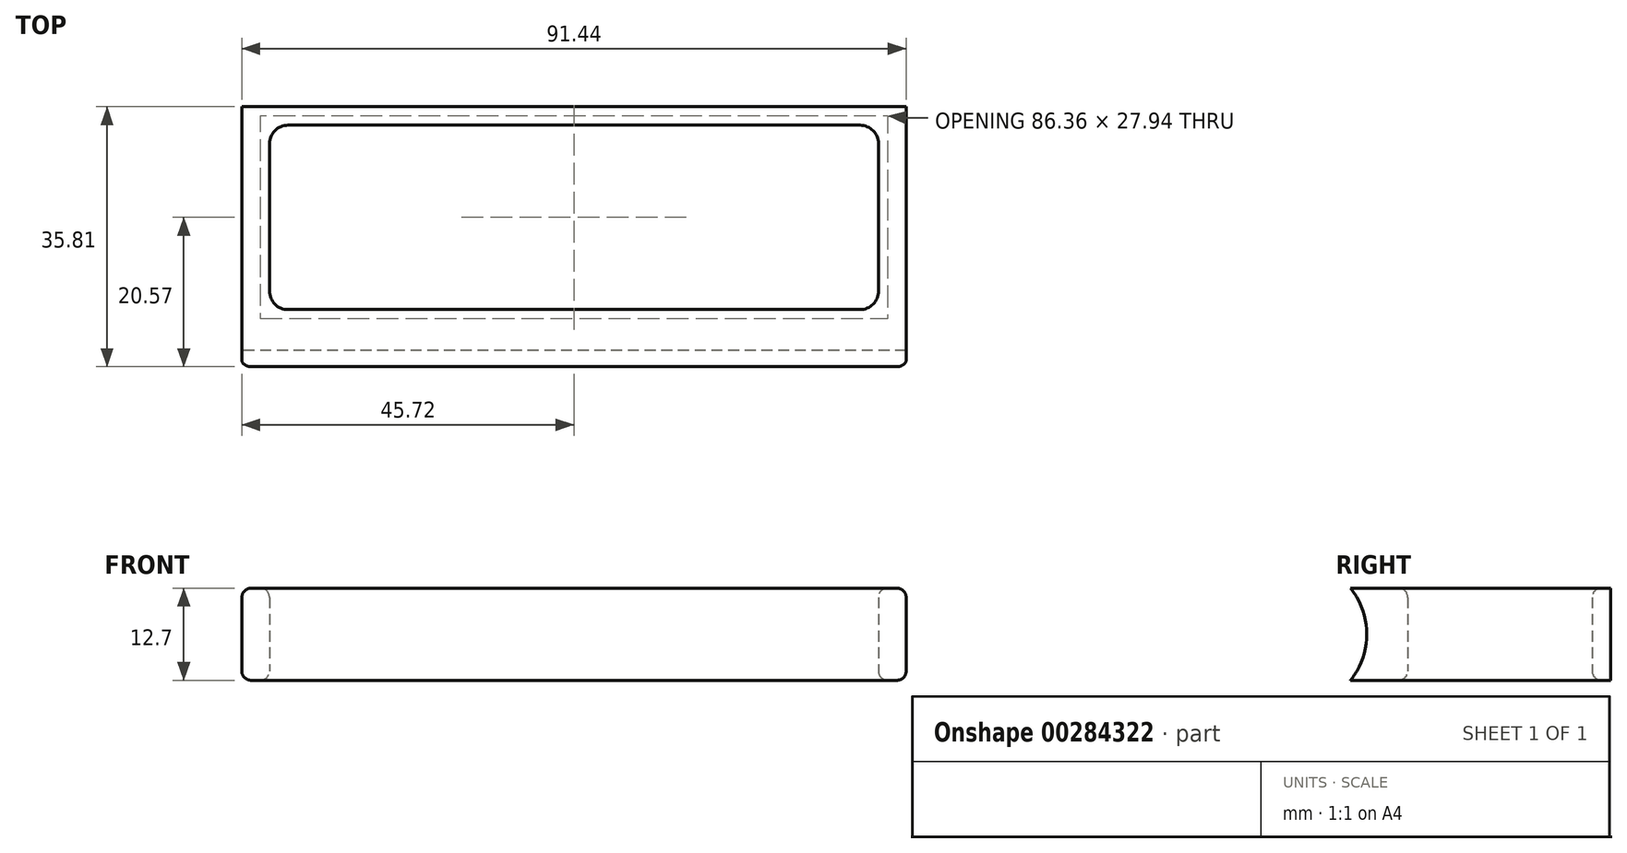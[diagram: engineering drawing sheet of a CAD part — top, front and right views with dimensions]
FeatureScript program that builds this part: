
annotation { "Feature Type Name" : "Feature", "Feature Type Description" : "" }
export const myFeature = defineFeature(function(context is Context, id is Id, definition is map)
    precondition{}
    {
        {
            var Q0;
            Q0=qCreatedBy(makeId("Top.planeOp"),FACE);
            var sketch = newSketch(context, id + "F0", { "sketchPlane" : qUnion([Q0])});
            skLineSegment(sketch, "E0", {"start": v(0, 0) * mm, "end": v(-45.72, 0) * mm});
            skLineSegment(sketch, "E1", {"start": v(0, 0) * mm, "end": v(45.72, 0) * mm});
            skLineSegment(sketch, "E2", {"start": v(-45.72, 0) * mm, "end": v(-45.72, -30.48) * mm});
            skLineSegment(sketch, "E3", {"start": v(-45.72, -30.48) * mm, "end": v(45.72, -30.48) * mm});
            skLineSegment(sketch, "E4", {"start": v(45.72, -30.48) * mm, "end": v(45.72, 0) * mm});
            skLineSegment(sketch, "E5", {"start": v(0, -30.48) * mm, "end": v(0, 0) * mm, "construction": true});
            skLineSegment(sketch, "E6.bottom", {"start": v(-41.91, -2.54) * mm, "end": v(41.91, -2.54) * mm});
            skLineSegment(sketch, "E6.top", {"start": v(-41.91, -27.94) * mm, "end": v(41.91, -27.94) * mm});
            skLineSegment(sketch, "E6.left", {"start": v(-41.91, -2.54) * mm, "end": v(-41.91, -27.94) * mm});
            skLineSegment(sketch, "E6.right", {"start": v(41.91, -2.54) * mm, "end": v(41.91, -27.94) * mm});
            skLineSegment(sketch, "E7", {"start": v(0, -2.54) * mm, "end": v(0, -27.94) * mm, "construction": true});
            skPoint(sketch, "E8", {"position": v(0, -15.24) * mm});
            skLineSegment(sketch, "E9.bottom", {"start": v(-1.27, -2.54) * mm, "end": v(1.27, -2.54) * mm});
            skLineSegment(sketch, "E9.top", {"start": v(-1.27, -27.94) * mm, "end": v(1.27, -27.94) * mm});
            skSolve(sketch);
        }
        {
            var Q0;
            Q0=makeQuery(id+"F0.imprint","IMPRINT",FACE,{"disambiguationData":[TD([[makeQuery(id+"F0.imprint","IMPRINT",EDGE,{"derivedFrom":sQuery(id+"F0.wireOp",EDGE,"E0")}),1.0]])]});
            extrude(context, id + "F1", {"entities" : qUnion([Q0]), "depth" : 12.7 * mm});
        }
        {
            var Q0;
            Q0=makeQuery(id+"F1.opExtrude","SWEPT_FACE",FACE,{"disambiguationData":[OSD([sQuery(id+"F0.wireOp",EDGE,"E4")])]});
            var sketch = newSketch(context, id + "F2", { "sketchPlane" : qUnion([Q0])});
            skLineSegment(sketch, "E10.0.0", {"start": v(-30.48, 0) * mm, "end": v(0, 0) * mm});
            skLineSegment(sketch, "E10.0.1", {"start": v(0, 0) * mm, "end": v(0, 12.7) * mm});
            skLineSegment(sketch, "E10.0.2", {"start": v(0, 12.7) * mm, "end": v(-30.48, 12.7) * mm});
            skLineSegment(sketch, "E10.0.3", {"start": v(-30.48, 12.7) * mm, "end": v(-30.48, 0) * mm});
            skArc(sketch, "E11", {"start": v(-0.6, 9.97) * mm, "mid": v(-0.08, 11.67) * mm, "end": v(-1.52, 12.7) * mm});
            skArc(sketch, "E12", {"start": v(-0.6, 7.56) * mm, "mid": v(0, 8.76) * mm, "end": v(-0.6, 9.97) * mm});
            skArc(sketch, "E13", {"start": v(-0.6, 5.14) * mm, "mid": v(0, 6.35) * mm, "end": v(-0.6, 7.56) * mm});
            skArc(sketch, "E14", {"start": v(-0.6, 2.73) * mm, "mid": v(0, 3.94) * mm, "end": v(-0.6, 5.14) * mm});
            skArc(sketch, "E15", {"start": v(-1.52, 0) * mm, "mid": v(-0.08, 1.03) * mm, "end": v(-0.6, 2.73) * mm});
            skLineSegment(sketch, "E16", {"start": v(-0.6, 0) * mm, "end": v(-0.6, 12.7) * mm, "construction": true});
            skLineSegment(sketch, "E17", {"start": v(-30.48, 0) * mm, "end": v(-35.8, 0) * mm});
            skLineSegment(sketch, "E18", {"start": v(-35.8, 0) * mm, "end": v(-30.48, 6.35) * mm});
            skLineSegment(sketch, "E19", {"start": v(-30.48, 6.35) * mm, "end": v(-35.8, 12.7) * mm});
            skLineSegment(sketch, "E20", {"start": v(-35.8, 12.7) * mm, "end": v(-30.48, 12.7) * mm});
            skSolve(sketch);
        }
        {
            var Q0;
            {var subQ2=sQuery(id+"F2.wireOp",EDGE,"E19");Q0=makeQuery(id+"F2.imprint","IMPRINT",FACE,{"disambiguationData":[TD([[makeQuery(id+"F2.imprint","IMPRINT",EDGE,{"derivedFrom":subQ2}),-1.0]])]});}
            var Q1;
            {var subQ0=sQuery(id+"F2.wireOp",EDGE,"E17");Q1=makeQuery(id+"F2.imprint","IMPRINT",FACE,{"disambiguationData":[TD([[makeQuery(id+"F2.imprint","IMPRINT",EDGE,{"derivedFrom":subQ0}),-1.0]])]});}
            var Q2;
            {var subQ0=sQuery(id+"F2.wireOp",EDGE,"E14");var subQ1=sQuery(id+"F2.wireOp",EDGE,"E10.0.1");var subQ2=sQuery(id+"F2.wireOp",EDGE,"E13");var subQ3=sQuery(id+"F2.wireOp",EDGE,"E12");Q2=makeQuery(id+"FTnoA9OfPemPWEm_1.1.Fb3Mo2sl9pyBsOD_1.boolean.opBoolean","MERGE",FACE,{"derivedFrom":[makeQuery(id+"F1.opExtrude","SWEPT_FACE",FACE,{"disambiguationData":[OSD([sQuery(id+"F0.wireOp",EDGE,"E2")])]}),makeQuery(id+"FTnoA9OfPemPWEm_1.1.Fb3Mo2sl9pyBsOD_1.opExtrude","CAP_FACE",FACE,{"disambiguationData":[OSD([subQ1,sQuery(id+"F2.wireOp",EDGE,"E11"),subQ3])],"isStart":true}),makeQuery(id+"FTnoA9OfPemPWEm_1.1.Fb3Mo2sl9pyBsOD_1.opExtrude","CAP_FACE",FACE,{"disambiguationData":[OSD([subQ1,subQ3,subQ2])],"isStart":true}),makeQuery(id+"FTnoA9OfPemPWEm_1.1.Fb3Mo2sl9pyBsOD_1.opExtrude","CAP_FACE",FACE,{"disambiguationData":[OSD([subQ1,subQ2,subQ0])],"isStart":true}),makeQuery(id+"FTnoA9OfPemPWEm_1.1.Fb3Mo2sl9pyBsOD_1.opExtrude","CAP_FACE",FACE,{"disambiguationData":[OSD([subQ1,subQ0,sQuery(id+"F2.wireOp",EDGE,"E15")])],"isStart":true})]});}
            extrude(context, id + "F3", {"entities" : qUnion([Q0, Q1]), "operationType" : NewBodyOperationType.ADD, "endBound" : BoundingType.UP_TO_SURFACE, "oppositeDirection" : true, "endBoundEntityFace" : qUnion([Q2]), "depth" : 101.6 * mm});
        }
        {
            var Q0;
            {var subQ0=sQuery(id+"F2.wireOp",EDGE,"E18");var subQ1=sQuery(id+"F2.wireOp",EDGE,"E10.0.3");var subQ2=sQuery(id+"F2.wireOp",EDGE,"E19");Q0=makeQuery(id+"F3.boolean.opBoolean","MERGE",EDGE,{"derivedFrom":[makeQuery(id+"F3.opExtrude","SWEPT_EDGE",EDGE,{"disambiguationData":[OSD([subQ1,subQ0,subQ2]),ownerDisambiguation([makeQuery(id+"F3.opExtrude","SWEPT_BODY",BODY,{"disambiguationData":[OSD([subQ1,subQ2,sQuery(id+"F2.wireOp",EDGE,"E20")])]})])]}),makeQuery(id+"F3.opExtrude","SWEPT_EDGE",EDGE,{"disambiguationData":[OSD([subQ1,subQ0,subQ2]),ownerDisambiguation([makeQuery(id+"F3.opExtrude","SWEPT_BODY",BODY,{"disambiguationData":[OSD([subQ1,sQuery(id+"F2.wireOp",EDGE,"E17"),subQ0])]})])]})]});}
            fillet(context, id + "F4", {"entities" : qUnion([Q0]), "radius" : 10.16 * mm, "tangentPropagation" : true, "allowEdgeOverflow" : false});
        }
        {
            var Q0;
            Q0=makeQuery(id+"F1.opExtrude","SWEPT_EDGE",EDGE,{"disambiguationData":[OSD([sQuery(id+"F0.wireOp",EDGE,"E6.top"),sQuery(id+"F0.wireOp",EDGE,"E6.left")])]});
            var Q1;
            Q1=makeQuery(id+"F1.opExtrude","SWEPT_EDGE",EDGE,{"disambiguationData":[OSD([sQuery(id+"F0.wireOp",EDGE,"E6.top"),sQuery(id+"F0.wireOp",EDGE,"E6.right")])]});
            var Q2;
            Q2=makeQuery(id+"F1.opExtrude","SWEPT_EDGE",EDGE,{"disambiguationData":[OSD([sQuery(id+"F0.wireOp",EDGE,"E6.bottom"),sQuery(id+"F0.wireOp",EDGE,"E6.right")])]});
            var Q3;
            Q3=makeQuery(id+"F1.opExtrude","SWEPT_EDGE",EDGE,{"disambiguationData":[OSD([sQuery(id+"F0.wireOp",EDGE,"E6.bottom"),sQuery(id+"F0.wireOp",EDGE,"E6.left")])]});
            var Q4;
            Q4=makeQuery(id+"F1.opExtrude","SWEPT_EDGE",EDGE,{"disambiguationData":[OSD([sQuery(id+"F0.wireOp",EDGE,"E6.bottom"),sQuery(id+"F0.wireOp",EDGE,"E9.bottom"),sQuery(id+"F0.wireOp",EDGE,"E9.left")])]});
            var Q5;
            Q5=makeQuery(id+"F1.opExtrude","SWEPT_EDGE",EDGE,{"disambiguationData":[OSD([sQuery(id+"F0.wireOp",EDGE,"E6.bottom"),sQuery(id+"F0.wireOp",EDGE,"E9.bottom"),sQuery(id+"F0.wireOp",EDGE,"E9.right")])]});
            var Q6;
            Q6=makeQuery(id+"F1.opExtrude","SWEPT_EDGE",EDGE,{"disambiguationData":[OSD([sQuery(id+"F0.wireOp",EDGE,"E6.top"),sQuery(id+"F0.wireOp",EDGE,"E9.top"),sQuery(id+"F0.wireOp",EDGE,"E9.right")])]});
            var Q7;
            Q7=makeQuery(id+"F1.opExtrude","SWEPT_EDGE",EDGE,{"disambiguationData":[OSD([sQuery(id+"F0.wireOp",EDGE,"E6.top"),sQuery(id+"F0.wireOp",EDGE,"E9.top"),sQuery(id+"F0.wireOp",EDGE,"E9.left")])]});
            fillet(context, id + "F5", {"entities" : qUnion([Q0, Q1, Q2, Q3, Q4, Q5, Q6, Q7]), "radius" : 2.54 * mm, "tangentPropagation" : true, "allowEdgeOverflow" : false});
        }
        {
            var Q0;
            Q0=qCreatedBy(makeId("Front.planeOp"),FACE);
            var Q1;
            Q1=sQuery(id+"F0.wireOp",VERTEX,"E8");
            cPlane(context, id + "F6", {"entities" : qUnion([Q0, Q1]), "cplaneType" : CPlaneType.PLANE_POINT, "offset" : 25.4 * mm, "width" : 152.4 * mm, "height" : 152.4 * mm});
        }
        {
            var Q0;
            Q0=makeQuery(id+"F1.opExtrude","CAP_EDGE",EDGE,{"disambiguationData":[OSD([sQuery(id+"F0.wireOp",EDGE,"E3")])],"isStart":false});
            var Q1;
            Q1=makeQuery(id+"F1.opExtrude","CAP_EDGE",EDGE,{"disambiguationData":[OSD([sQuery(id+"F0.wireOp",EDGE,"E3")])],"isStart":true});
            var Q2;
            Q2=makeQuery(id+"F1.opExtrude","CAP_EDGE",EDGE,{"disambiguationData":[OSD([sQuery(id+"F0.wireOp",EDGE,"E4")])],"isStart":false});
            var Q3;
            Q3=makeQuery(id+"F1.opExtrude","SWEPT_EDGE",EDGE,{"disambiguationData":[OSD([sQuery(id+"F0.wireOp",EDGE,"E3"),sQuery(id+"F0.wireOp",EDGE,"E4")])]});
            var Q4;
            Q4=makeQuery(id+"F1.opExtrude","SWEPT_EDGE",EDGE,{"disambiguationData":[OSD([sQuery(id+"F0.wireOp",EDGE,"E2"),sQuery(id+"F0.wireOp",EDGE,"E3")])]});
            var Q5;
            Q5=makeQuery(id+"F1.opExtrude","CAP_EDGE",EDGE,{"disambiguationData":[OSD([sQuery(id+"F0.wireOp",EDGE,"E2")])],"isStart":false});
            var Q6;
            Q6=makeQuery(id+"F1.opExtrude","CAP_EDGE",EDGE,{"disambiguationData":[OSD([sQuery(id+"F0.wireOp",EDGE,"E2")])],"isStart":true});
            var Q7;
            Q7=makeQuery(id+"F3.opExtrude","SWEPT_EDGE",EDGE,{"disambiguationData":[OSD([sQuery(id+"F2.wireOp",EDGE,"E19"),sQuery(id+"F2.wireOp",EDGE,"E20")])]});
            var Q8;
            Q8=makeQuery(id+"F3.opExtrude","SWEPT_EDGE",EDGE,{"disambiguationData":[OSD([sQuery(id+"F2.wireOp",EDGE,"E17"),sQuery(id+"F2.wireOp",EDGE,"E18")])]});
            var Q9;
            Q9=makeQuery(id+"F3.opExtrude","CAP_EDGE",EDGE,{"disambiguationData":[OSD([sQuery(id+"F2.wireOp",EDGE,"E19")])],"isStart":false});
            var Q10;
            Q10=makeQuery(id+"F3.opExtrude","CAP_EDGE",EDGE,{"disambiguationData":[OSD([sQuery(id+"F2.wireOp",EDGE,"E19")])],"isStart":true});
            var Q11;
            {var subQ0=sQuery(id+"F2.wireOp",EDGE,"E17");Q11=makeQuery(id+"FvgQqoOcXEQCqVI_1.1.F3.boolean.opBoolean","MERGE",EDGE,{"derivedFrom":[makeQuery(id+"F3.boolean.opBoolean","MERGE",EDGE,{"derivedFrom":[makeQuery(id+"F1.opExtrude","CAP_EDGE",EDGE,{"disambiguationData":[OSD([sQuery(id+"F0.wireOp",EDGE,"E4")])],"isStart":true}),makeQuery(id+"F3.opExtrude","CAP_EDGE",EDGE,{"disambiguationData":[OSD([subQ0])],"isStart":true})]}),makeQuery(id+"FvgQqoOcXEQCqVI_1.1.F3.opExtrude","CAP_EDGE",EDGE,{"disambiguationData":[OSD([subQ0])],"isStart":true})]});}
            var Q12;
            Q12=makeQuery(id+"F1.opExtrude","CAP_EDGE",EDGE,{"disambiguationData":[OSD([sQuery(id+"F0.wireOp",EDGE,"E6.top"),sQuery(id+"F0.wireOp",EDGE,"E9.top")])],"isStart":true});
            var Q13;
            Q13=makeQuery(id+"F1.opExtrude","CAP_EDGE",EDGE,{"disambiguationData":[OSD([sQuery(id+"F0.wireOp",EDGE,"E6.left")])],"isStart":false});
            fillet(context, id + "F7", {"entities" : qUnion([Q0, Q1, Q2, Q3, Q4, Q5, Q6, Q7, Q8, Q9, Q10, Q11, Q12, Q13]), "radius" : 1.27 * mm, "tangentPropagation" : true, "allowEdgeOverflow" : false});
        }
    });
